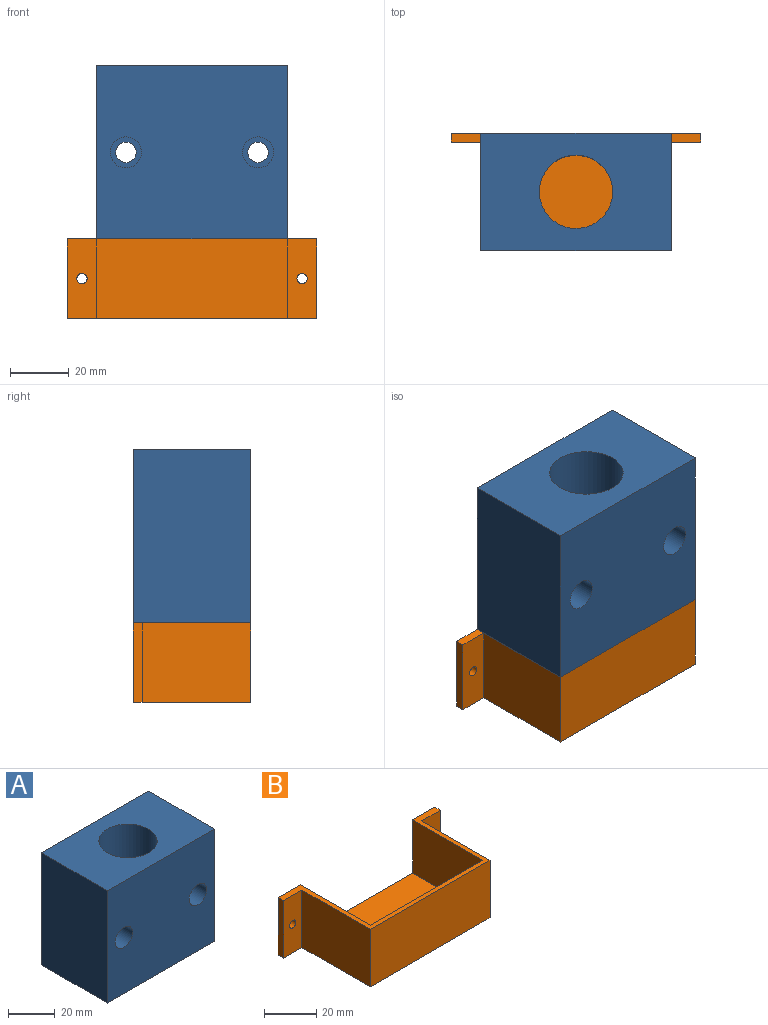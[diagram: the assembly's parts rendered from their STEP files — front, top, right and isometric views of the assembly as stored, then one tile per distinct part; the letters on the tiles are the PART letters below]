
ASSEMBLY  parts=2 mates=1
PART A: 27 faces, bbox 65x40x59 mm
  f0: cylinder r=3.5mm len=24.4mm, axis (0,-1,0), area 536.6mm2, adj f12,f26
  f1: cylinder r=3.5mm len=24.4mm, axis (0,-1,0), area 536.6mm2, adj f10,f19
  f2: plane 65x59mm, normal (0,1,0), area 3629.2mm2, adj f4,f5,f6,f7,f13,f14,f15,f16
  f3: plane 65x59mm, normal (0,-1,0), area 3658.5mm2, adj f4,f5,f6,f7,f9,f11
  f4: plane 65x40mm, normal (0,0,1), area 2109.1mm2, adj f2,f3,f5,f7,f8
  f5: plane 59x40mm, normal (-1,0,0), area 2360mm2, adj f2,f3,f4,f6
  f6: plane 65x40mm, normal (0,0,-1), area 2109.1mm2, adj f2,f3,f5,f7,f8
  f7: plane 59x40mm, normal (1,0,0), area 2360mm2, adj f2,f3,f4,f6
  f8: cylinder r=12.5mm len=59mm, axis (0,0,1), area 4633.8mm2, adj f4,f6
  f9: cylinder r=5.3mm len=10.6mm, axis (0,-1,0), area 333mm2, adj f3,f10
  f10: plane 10.6x10.6mm, normal (0,-1,0), area 49.8mm2, adj f1,f9
  f11: cylinder r=5.3mm len=10.6mm, axis (0,-1,0), area 333mm2, adj f3,f12
  f12: plane 10.6x10.6mm, normal (0,-1,0), area 49.8mm2, adj f0,f11
  f13: plane 5.6x5.45mm, normal (0.5,0,-0.87), area 35.2mm2, adj f2,f14,f18,f19
  f14: plane 5.6x5.45mm, normal (-0.5,0,-0.87), area 35.2mm2, adj f2,f13,f15,f19
  f15: plane 6.29x5.6mm, normal (-1,0,0), area 35.2mm2, adj f2,f14,f16,f19
  f16: plane 5.6x5.45mm, normal (-0.5,0,0.87), area 35.2mm2, adj f2,f15,f17,f19
  f17: plane 5.6x5.45mm, normal (0.5,0,0.87), area 35.2mm2, adj f2,f16,f18,f19
  f18: plane 6.29x5.6mm, normal (1,0,0), area 35.2mm2, adj f2,f13,f17,f19
  f19: plane 12.59x10.9mm, normal (0,1,0), area 64.4mm2, adj f1,f13,f14,f15,f16,f17,f18
  f20: plane 6.29x5.6mm, normal (1,0,0), area 35.2mm2, adj f2,f21,f25,f26
  f21: plane 5.6x5.45mm, normal (0.5,0,-0.87), area 35.2mm2, adj f2,f20,f22,f26
  f22: plane 5.6x5.45mm, normal (-0.5,0,-0.87), area 35.2mm2, adj f2,f21,f23,f26
  f23: plane 6.29x5.6mm, normal (-1,0,0), area 35.2mm2, adj f2,f22,f24,f26
  f24: plane 5.6x5.45mm, normal (-0.5,0,0.87), area 35.2mm2, adj f2,f23,f25,f26
  f25: plane 5.6x5.45mm, normal (0.5,0,0.87), area 35.2mm2, adj f2,f20,f24,f26
  f26: plane 12.59x10.9mm, normal (0,1,0), area 64.4mm2, adj f0,f20,f21,f22,f23,f24,f25
PART B: 16 faces, bbox 85x40x27 mm
  f0: plane 85x27mm, normal (0,1,0), area 750.8mm2, adj f2,f5,f6,f7,f9,f11,f13,f14
  f1: plane 37x27mm, normal (-1,0,0), area 999mm2, adj f3,f5,f9,f10
  f2: plane 61x38mm, normal (0,0,1), area 2318mm2, adj f0,f6,f7,f8
  f3: plane 65x27mm, normal (0,-1,0), area 1755mm2, adj f1,f4,f5,f9
  f4: plane 37x27mm, normal (1,0,0), area 999mm2, adj f3,f5,f9,f12
  f5: plane 85x40mm, normal (0,0,-1), area 2660mm2, adj f0,f1,f3,f4,f10,f11,f12,f13
  f6: plane 38x25mm, normal (1,0,0), area 950mm2, adj f0,f2,f8,f9
  f7: plane 38x25mm, normal (-1,0,0), area 950mm2, adj f0,f2,f8,f9
  f8: plane 61x25mm, normal (0,1,0), area 1525mm2, adj f2,f6,f7,f9
  f9: plane 85x40mm, normal (0,0,1), area 342mm2, adj f0,f1,f3,f4,f6,f7,f8,f10
  f10: plane 27x10mm, normal (0,-1,0), area 260.4mm2, adj f1,f5,f9,f11,f15
  f11: plane 27x3mm, normal (-1,0,0), area 81mm2, adj f0,f5,f9,f10
  f12: plane 27x10mm, normal (0,-1,0), area 260.4mm2, adj f4,f5,f9,f13,f14
  f13: plane 27x3mm, normal (1,0,0), area 81mm2, adj f0,f5,f9,f12
  f14: cylinder r=1.75mm len=3.5mm, axis (0,-1,0), area 33mm2, adj f0,f12
  f15: cylinder r=1.75mm len=3.5mm, axis (0,-1,0), area 33mm2, adj f0,f10
PLACE A at identity
PLACE B t=(0,-20,-56.5)mm
MATE planar B.f9 <-> A.f6  axis (0,0,1) through (32.5,-40,-29.5)mm
